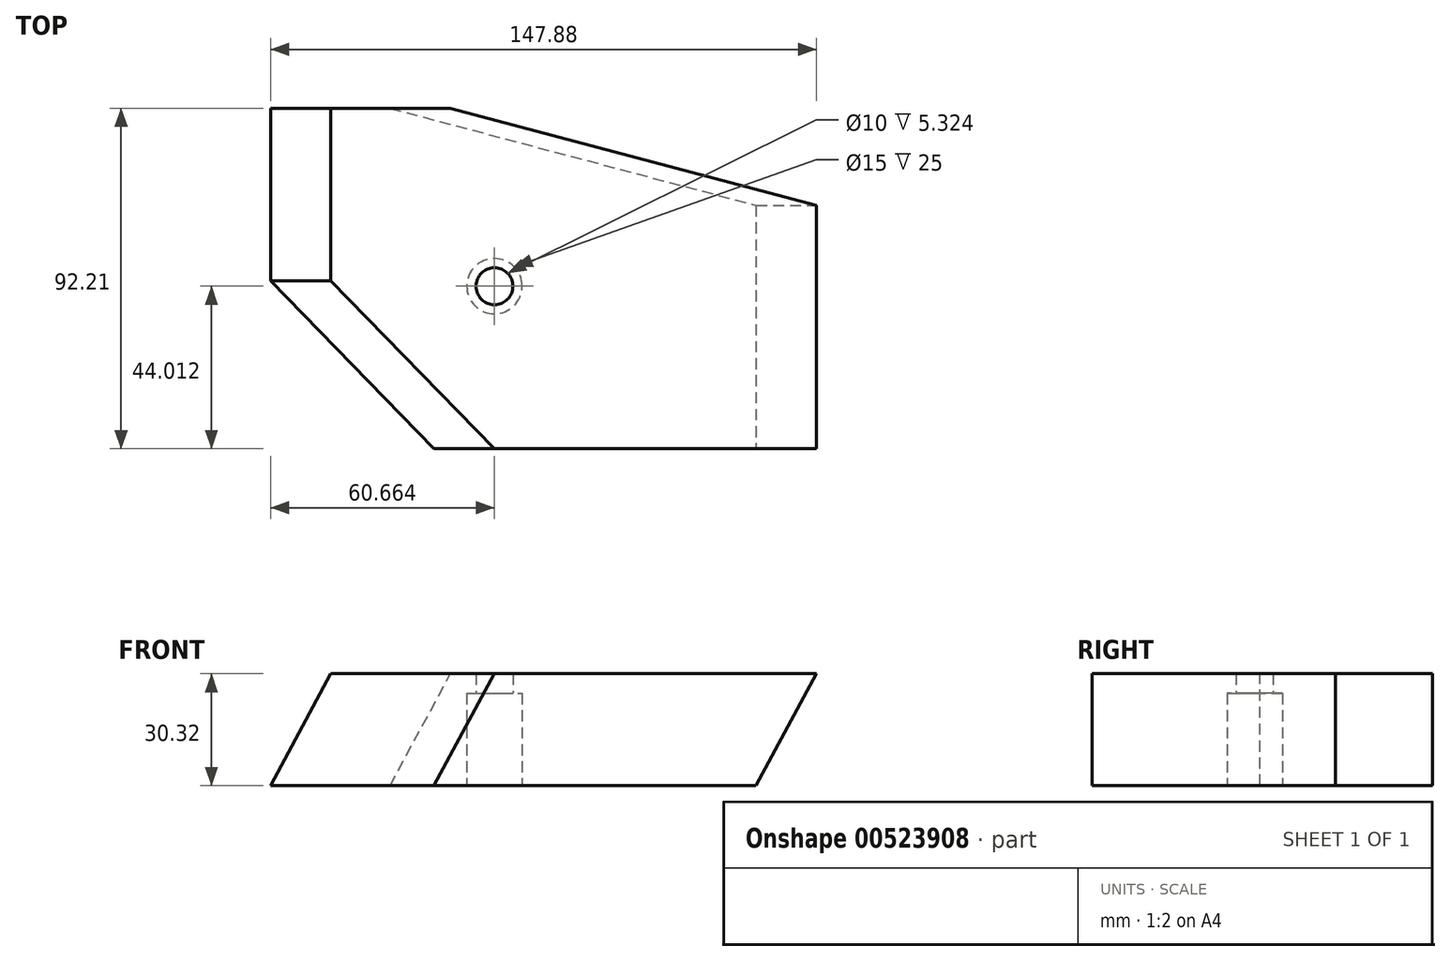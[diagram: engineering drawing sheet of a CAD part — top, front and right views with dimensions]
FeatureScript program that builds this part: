
annotation { "Feature Type Name" : "Feature", "Feature Type Description" : "" }
export const myFeature = defineFeature(function(context is Context, id is Id, definition is map)
    precondition{}
    {
        {
            var Q0;
            Q0=qCreatedBy(makeId("Top.planeOp"),FACE);
            var sketch = newSketch(context, id + "F0", { "sketchPlane" : qUnion([Q0])});
            skLineSegment(sketch, "E0.bottom", {"start": v(-40.15, 31.99) * mm, "end": v(47.08, 31.99) * mm});
            skLineSegment(sketch, "E0.top", {"start": v(-40.15, -33.92) * mm, "end": v(47.08, -33.92) * mm});
            skLineSegment(sketch, "E0.left", {"start": v(-40.15, 31.99) * mm, "end": v(-40.15, -33.92) * mm});
            skLineSegment(sketch, "E0.right", {"start": v(47.08, 31.99) * mm, "end": v(47.08, -33.92) * mm});
            skLineSegment(sketch, "E1.bottom", {"start": v(-84.46, 58.3) * mm, "end": v(-52.06, 58.3) * mm});
            skLineSegment(sketch, "E1.top", {"start": v(-84.46, 11.5) * mm, "end": v(-52.06, 11.5) * mm});
            skLineSegment(sketch, "E1.left", {"start": v(-84.46, 58.3) * mm, "end": v(-84.46, 11.5) * mm});
            skLineSegment(sketch, "E1.right", {"start": v(-52.06, 58.3) * mm, "end": v(-52.06, 11.5) * mm});
            skLineSegment(sketch, "E2", {"start": v(-84.46, 11.5) * mm, "end": v(-40.15, -33.92) * mm});
            skLineSegment(sketch, "E3", {"start": v(-52.06, 58.3) * mm, "end": v(47.08, 31.99) * mm});
            skSolve(sketch);
        }
        {
            var Q0;
            Q0=qCreatedBy(makeId("Front.planeOp"),FACE);
            var sketch = newSketch(context, id + "F1", { "sketchPlane" : qUnion([Q0])});
            skLineSegment(sketch, "E4", {"start": v(3.32, 0) * mm, "end": v(19.66, 30.32) * mm});
            skSolve(sketch);
        }
        {
            var Q0;
            Q0 = qSketchRegion(id + "F0", true);
            var Q1;
            Q1 = qConstructionFilter(qBodyType(qCreatedBy(id + "F1" ,EDGE), BodyType.WIRE), ConstructionObject.NO);
            sweep(context, id + "F2", {"profiles" : qUnion([Q0]), "path" : qUnion([Q1])});
        }
        {
            var Q0;
            Q0=makeQuery(id+"F2.opSweep","CAP_FACE",FACE,{"disambiguationData":[OSD([sQuery(id+"F0.wireOp",EDGE,"E0.top"),sQuery(id+"F0.wireOp",EDGE,"E0.right"),sQuery(id+"F0.wireOp",EDGE,"E1.bottom"),sQuery(id+"F0.wireOp",EDGE,"E1.left"),sQuery(id+"F0.wireOp",EDGE,"E2"),sQuery(id+"F0.wireOp",EDGE,"E3"),sQuery(id+"F1.wireOp",VERTEX,"E4.start")])],"isStart":true});
            var sketch = newSketch(context, id + "F3", { "sketchPlane" : qUnion([Q0])});
            skPoint(sketch, "E5", {"position": v(-23.8, -10.1) * mm});
            skSolve(sketch);
        }
        {
            var Q0;
            Q0=sQuery(id+"F3.wireOp",VERTEX,"E5");
            var Q1;
            Q1=makeQuery(id+"F2.opSweep","SWEPT_BODY",BODY,{"disambiguationData":[OSD([sQuery(id+"F0.wireOp",EDGE,"E0.top"),sQuery(id+"F0.wireOp",EDGE,"E0.right"),sQuery(id+"F0.wireOp",EDGE,"E1.bottom"),sQuery(id+"F0.wireOp",EDGE,"E1.left"),sQuery(id+"F0.wireOp",EDGE,"E2"),sQuery(id+"F0.wireOp",EDGE,"E3"),sQuery(id+"F1.wireOp",EDGE,"E4")])]});
            hole(context, id + "F4", {"style" : HoleStyle.C_BORE, "endStyle" : HoleEndStyle.THROUGH, "holeDiameter" : 10 * mm, "cBoreDiameter" : 15 * mm, "cBoreDepth" : 25 * mm, "isTappedThrough" : true, "tappedDepth" : 12 * mm, "tapClearance" : 3, "startFromSketch" : true, "locations" : qUnion([Q0]), "scope" : qUnion([Q1])});
        }
    });
